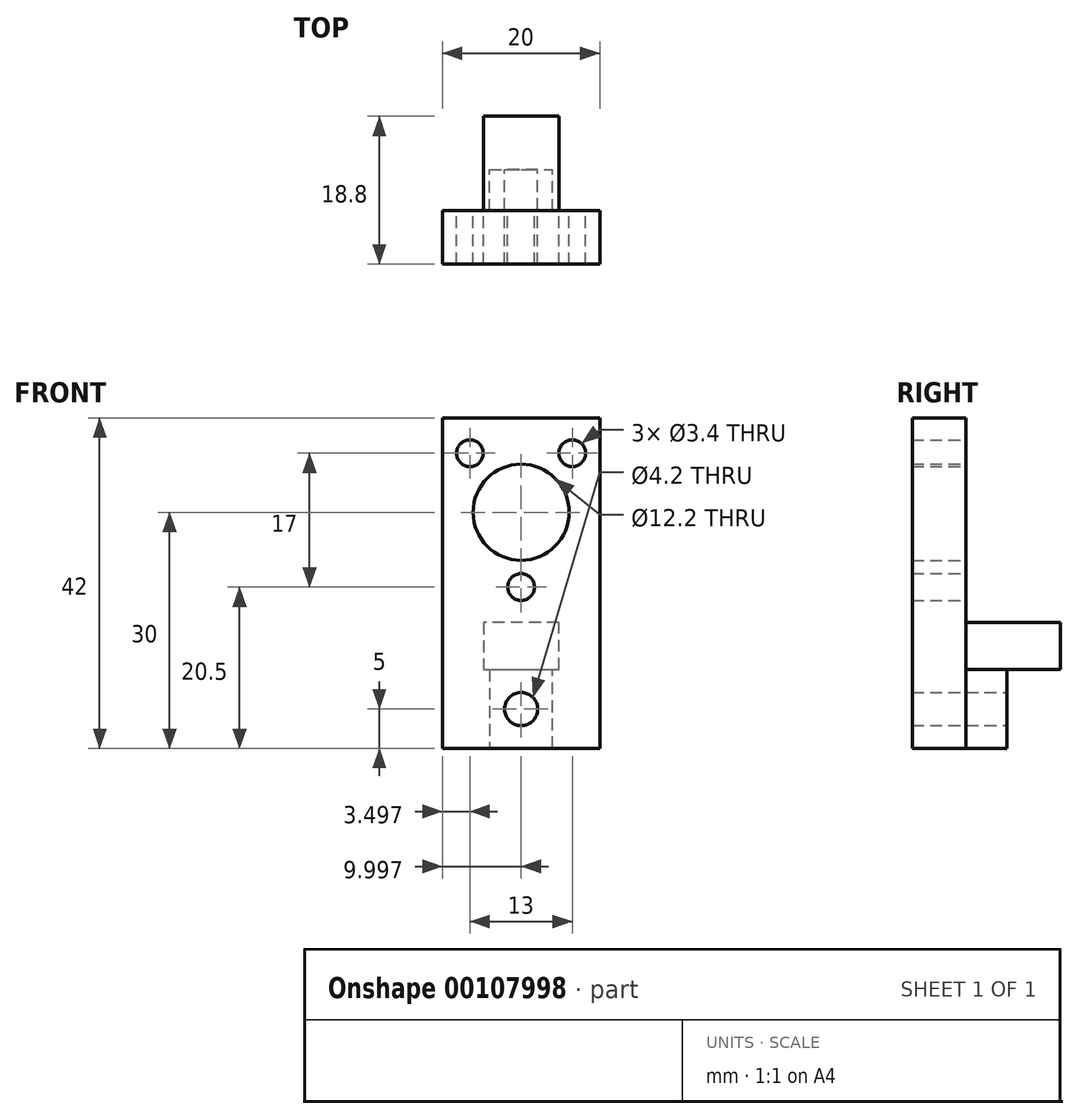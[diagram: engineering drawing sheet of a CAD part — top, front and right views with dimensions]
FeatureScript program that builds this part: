
annotation { "Feature Type Name" : "Feature", "Feature Type Description" : "" }
export const myFeature = defineFeature(function(context is Context, id is Id, definition is map)
    precondition{}
    {
        {
            var Q0;
            Q0=qCreatedBy(makeId("Front.planeOp"),FACE);
            var sketch = newSketch(context, id + "F0", { "sketchPlane" : qUnion([Q0])});
            skCircle(sketch, "E0", {"center": v(11.29, 30) * mm, "radius": 6.1 * mm});
            skPoint(sketch, "E0.centerSnap0", {"position": v(11.29, 60.28) * mm});
            skCircle(sketch, "E1", {"center": v(17.79, 37.5) * mm, "radius": 1.7 * mm});
            skCircle(sketch, "E2", {"center": v(4.79, 37.5) * mm, "radius": 1.7 * mm});
            skCircle(sketch, "E3", {"center": v(11.29, 20.5) * mm, "radius": 1.7 * mm});
            skLineSegment(sketch, "E4", {"start": v(1.29, 31.58) * mm, "end": v(1.29, 16) * mm});
            skLineSegment(sketch, "E5", {"start": v(1.29, 16) * mm, "end": v(7.29, 16) * mm});
            skLineSegment(sketch, "E6", {"start": v(7.29, 16) * mm, "end": v(7.29, 0) * mm});
            skLineSegment(sketch, "E7", {"start": v(15.29, 0) * mm, "end": v(15.29, 16) * mm});
            skLineSegment(sketch, "E8", {"start": v(15.29, 16) * mm, "end": v(21.29, 16) * mm});
            skLineSegment(sketch, "E9", {"start": v(21.29, 16) * mm, "end": v(21.29, 31.58) * mm});
            skLineSegment(sketch, "E10", {"start": v(1.29, 31.58) * mm, "end": v(1.29, 42) * mm});
            skLineSegment(sketch, "E11", {"start": v(1.29, 42) * mm, "end": v(21.29, 42) * mm});
            skLineSegment(sketch, "E12", {"start": v(21.29, 42) * mm, "end": v(21.29, 31.58) * mm});
            skLineSegment(sketch, "E13", {"start": v(7.29, 0) * mm, "end": v(15.29, 0) * mm});
            skCircle(sketch, "E14", {"center": v(11.29, 5) * mm, "radius": 2.1 * mm});
            skPoint(sketch, "E14.centerSnap0", {"position": v(11.29, 0) * mm});
            skLineSegment(sketch, "E15.bottom", {"start": v(6.49, 16) * mm, "end": v(7.29, 16) * mm});
            skLineSegment(sketch, "E15.top", {"start": v(6.49, 10) * mm, "end": v(7.29, 10) * mm});
            skLineSegment(sketch, "E15.left", {"start": v(6.49, 16) * mm, "end": v(6.49, 10) * mm});
            skLineSegment(sketch, "E15.right", {"start": v(7.29, 16) * mm, "end": v(7.29, 10) * mm});
            skLineSegment(sketch, "E16.bottom", {"start": v(15.29, 10) * mm, "end": v(16.09, 10) * mm});
            skLineSegment(sketch, "E16.top", {"start": v(15.29, 16) * mm, "end": v(16.09, 16) * mm});
            skLineSegment(sketch, "E16.left", {"start": v(15.29, 10) * mm, "end": v(15.29, 16) * mm});
            skLineSegment(sketch, "E16.right", {"start": v(16.09, 10) * mm, "end": v(16.09, 16) * mm});
            skSolve(sketch);
        }
        {
            var Q0;
            Q0 = qSketchRegion(id + "F0", true);
            var Q1;
            Q1=makeQuery(id+"F0.imprint","IMPRINT",FACE,{"disambiguationData":[TD([[makeQuery(id+"F0.imprint","IMPRINT",EDGE,{"derivedFrom":sQuery(id+"F0.wireOp",EDGE,"E0")}),-1.0]])]});
            extrude(context, id + "F1", {"entities" : qUnion([Q0, Q1]), "depth" : (12 + 6) * mm});
        }
        {
            var Q0;
            Q0=makeQuery(id+"F1.opExtrude","SWEPT_FACE",FACE,{"disambiguationData":[OSD([sQuery(id+"F0.wireOp",EDGE,"E9"),sQuery(id+"F0.wireOp",EDGE,"E12")])]});
            var sketch = newSketch(context, id + "F2", { "sketchPlane" : qUnion([Q0])});
            skLineSegment(sketch, "E17.bottom", {"start": v(0, 16) * mm, "end": v(-6, 16) * mm});
            skLineSegment(sketch, "E17.top", {"start": v(0, 0) * mm, "end": v(-6, 0) * mm});
            skLineSegment(sketch, "E17.left", {"start": v(0, 16) * mm, "end": v(0, 0) * mm});
            skLineSegment(sketch, "E17.right", {"start": v(-6, 16) * mm, "end": v(-6, 0) * mm});
            skLineSegment(sketch, "E18.bottom", {"start": v(-6, 16) * mm, "end": v(0, 16) * mm});
            skLineSegment(sketch, "E18.top", {"start": v(-6, 10) * mm, "end": v(0, 10) * mm});
            skLineSegment(sketch, "E18.left", {"start": v(-6, 16) * mm, "end": v(-6, 10) * mm});
            skLineSegment(sketch, "E18.right", {"start": v(0, 16) * mm, "end": v(0, 10) * mm});
            skSolve(sketch);
        }
        {
            var Q0;
            Q0=makeQuery(id+"F2.imprint","IMPRINT",FACE,{"disambiguationData":[TD([[makeQuery(id+"F2.imprint","IMPRINT",EDGE,{"derivedFrom":sQuery(id+"F2.wireOp",EDGE,"E17.top")}),-1.0]])]});
            extrude(context, id + "F3", {"entities" : qUnion([Q0]), "operationType" : NewBodyOperationType.REMOVE, "endBound" : BoundingType.THROUGH_ALL, "oppositeDirection" : true, "depth" : 25 * mm});
        }
        {
            var Q0;
            Q0=makeQuery(id+"F1.opExtrude","CAP_FACE",FACE,{"disambiguationData":[OSD([sQuery(id+"F0.wireOp",EDGE,"E0"),sQuery(id+"F0.wireOp",EDGE,"E1"),sQuery(id+"F0.wireOp",EDGE,"E2"),sQuery(id+"F0.wireOp",EDGE,"E3"),sQuery(id+"F0.wireOp",EDGE,"E4"),sQuery(id+"F0.wireOp",EDGE,"E5"),sQuery(id+"F0.wireOp",EDGE,"E6"),sQuery(id+"F0.wireOp",EDGE,"E7"),sQuery(id+"F0.wireOp",EDGE,"E8"),sQuery(id+"F0.wireOp",EDGE,"E9"),sQuery(id+"F0.wireOp",EDGE,"E10"),sQuery(id+"F0.wireOp",EDGE,"E11"),sQuery(id+"F0.wireOp",EDGE,"E12"),sQuery(id+"F0.wireOp",EDGE,"E13"),sQuery(id+"F0.wireOp",EDGE,"E14")])],"isStart":true});
            extrude(context, id + "F4", {"entities" : qUnion([Q0]), "operationType" : NewBodyOperationType.REMOVE, "oppositeDirection" : true, "depth" : (6 - 0.8) * mm});
        }
        {
            var Q0;
            Q0=makeQuery(id+"F4.boolean.opBoolean","COPY",FACE,{"derivedFrom":makeQuery(id+"F4.opExtrude","CAP_FACE",FACE,{"disambiguationData":[OSD([sQuery(id+"F0.wireOp",EDGE,"E0"),sQuery(id+"F0.wireOp",EDGE,"E1"),sQuery(id+"F0.wireOp",EDGE,"E2"),sQuery(id+"F0.wireOp",EDGE,"E3"),sQuery(id+"F0.wireOp",EDGE,"E4"),sQuery(id+"F0.wireOp",EDGE,"E5"),sQuery(id+"F0.wireOp",EDGE,"E6"),sQuery(id+"F0.wireOp",EDGE,"E7"),sQuery(id+"F0.wireOp",EDGE,"E8"),sQuery(id+"F0.wireOp",EDGE,"E9"),sQuery(id+"F0.wireOp",EDGE,"E10"),sQuery(id+"F0.wireOp",EDGE,"E11"),sQuery(id+"F0.wireOp",EDGE,"E12"),sQuery(id+"F0.wireOp",EDGE,"E13"),sQuery(id+"F0.wireOp",EDGE,"E14")])],"isStart":false})});
            var sketch = newSketch(context, id + "F5", { "sketchPlane" : qUnion([Q0])});
            skLineSegment(sketch, "E19.bottom", {"start": v(-30.72, 16) * mm, "end": v(6.67, 16) * mm});
            skLineSegment(sketch, "E19.top", {"start": v(-30.72, 49.94) * mm, "end": v(6.67, 49.94) * mm});
            skLineSegment(sketch, "E19.left", {"start": v(-30.72, 16) * mm, "end": v(-30.72, 49.94) * mm});
            skLineSegment(sketch, "E19.right", {"start": v(6.67, 16) * mm, "end": v(6.67, 49.94) * mm});
            skSolve(sketch);
        }
        {
            var Q0;
            Q0 = qSketchRegion(id + "F5", true);
            extrude(context, id + "F6", {"entities" : qUnion([Q0]), "operationType" : NewBodyOperationType.REMOVE, "oppositeDirection" : true, "depth" : 6 * mm});
        }
        {
            var Q0;
            Q0=makeQuery(id+"F4.boolean.opBoolean","COPY",FACE,{"derivedFrom":makeQuery(id+"F4.opExtrude","CAP_FACE",FACE,{"disambiguationData":[OSD([sQuery(id+"F0.wireOp",EDGE,"E0"),sQuery(id+"F0.wireOp",EDGE,"E1"),sQuery(id+"F0.wireOp",EDGE,"E2"),sQuery(id+"F0.wireOp",EDGE,"E3"),sQuery(id+"F0.wireOp",EDGE,"E4"),sQuery(id+"F0.wireOp",EDGE,"E5"),sQuery(id+"F0.wireOp",EDGE,"E6"),sQuery(id+"F0.wireOp",EDGE,"E7"),sQuery(id+"F0.wireOp",EDGE,"E8"),sQuery(id+"F0.wireOp",EDGE,"E9"),sQuery(id+"F0.wireOp",EDGE,"E10"),sQuery(id+"F0.wireOp",EDGE,"E11"),sQuery(id+"F0.wireOp",EDGE,"E12"),sQuery(id+"F0.wireOp",EDGE,"E13"),sQuery(id+"F0.wireOp",EDGE,"E14")])],"isStart":false})});
            extrude(context, id + "F7", {"entities" : qUnion([Q0]), "operationType" : NewBodyOperationType.ADD, "depth" : 6 * mm});
        }
        {
            var Q0;
            Q0=makeQuery(id+"F1.opExtrude","SWEPT_FACE",FACE,{"disambiguationData":[OSD([sQuery(id+"F0.wireOp",EDGE,"E5")])]});
            var sketch = newSketch(context, id + "F8", { "sketchPlane" : qUnion([Q0])});
            skLineSegment(sketch, "E20.bottom", {"start": v(1.29, 18) * mm, "end": v(21.29, 18) * mm});
            skLineSegment(sketch, "E20.top", {"start": v(1.29, 11.2) * mm, "end": v(21.29, 11.2) * mm});
            skLineSegment(sketch, "E20.left", {"start": v(1.29, 18) * mm, "end": v(1.29, 11.2) * mm});
            skLineSegment(sketch, "E20.right", {"start": v(21.29, 18) * mm, "end": v(21.29, 11.2) * mm});
            skSolve(sketch);
        }
        {
            var Q0;
            Q0 = qSketchRegion(id + "F8", true);
            extrude(context, id + "F9", {"entities" : qUnion([Q0]), "operationType" : NewBodyOperationType.ADD, "depth" : 16 * mm});
        }
        {
            var Q0;
            Q0=makeQuery(id+"F0.imprint","IMPRINT",FACE,{"disambiguationData":[TD([[makeQuery(id+"F0.imprint","IMPRINT",EDGE,{"derivedFrom":sQuery(id+"F0.wireOp",EDGE,"E14")}),1.0]])]});
            extrude(context, id + "F10", {"entities" : qUnion([Q0]), "operationType" : NewBodyOperationType.REMOVE, "endBound" : BoundingType.THROUGH_ALL, "depth" : 25 * mm});
        }
    });
